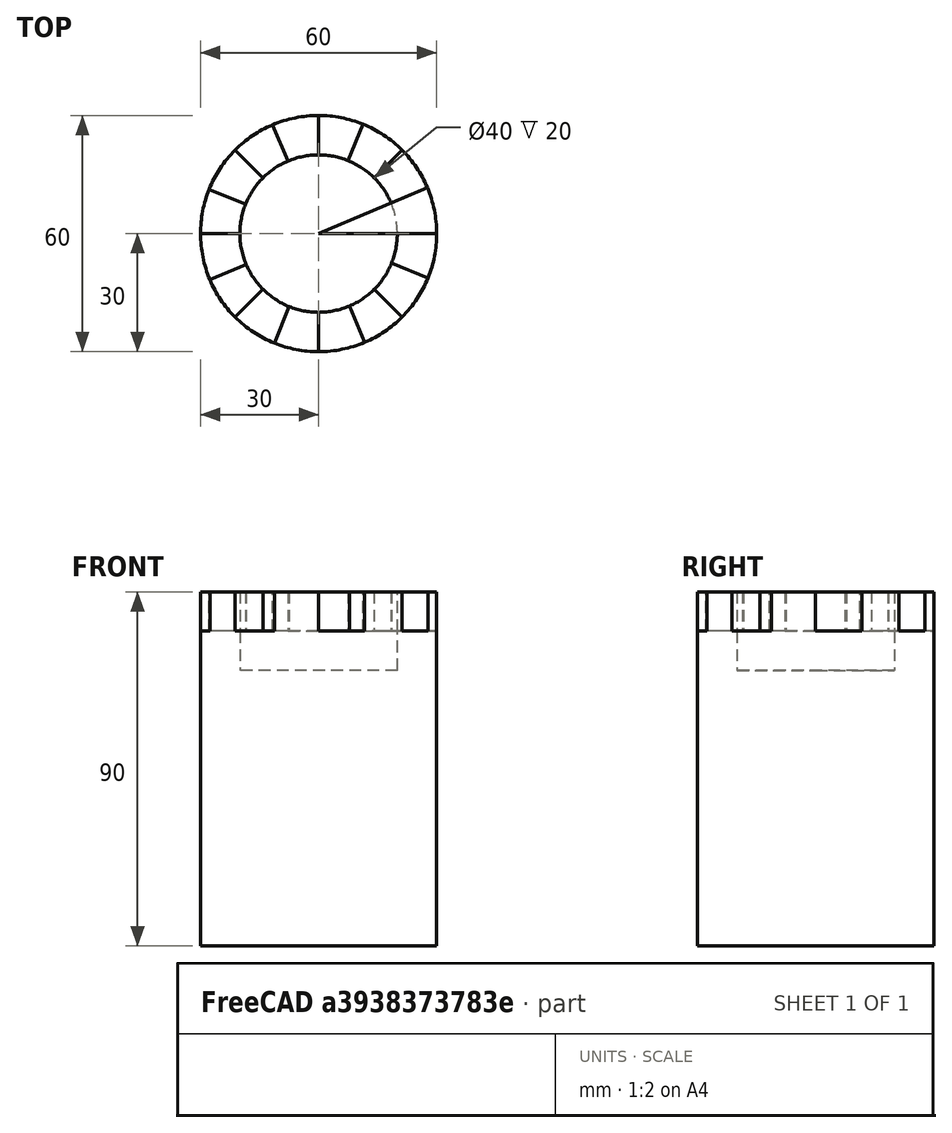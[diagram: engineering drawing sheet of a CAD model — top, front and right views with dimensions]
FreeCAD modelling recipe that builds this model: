
FCSTD DOCUMENT  (FreeCAD 0.21R33694 (Git))
Label: OJT1_T11R03_castell
License: All rights reserved
LicenseURL: http://en.wikipedia.org/wiki/All_rights_reserved
objects: Part::Cylinder×3, Part::Cut×2, Part::FeaturePython×1
note: 5 computed .brp shape members not serialized (recipe doc carries the construction recipe); baked Part::Feature solids carry a one-line shape summary decoded from their .brp

FEATURE [Part::Cylinder] Cylinder
  Angle = 360
  AttacherType = Attacher::AttachEngine3D
  FirstAngle = 0
  Height = 90
  Radius = 30
  SecondAngle = 0
FEATURE [Part::Cylinder] Cylinder001
  Angle = 23
  AttacherType = Attacher::AttachEngine3D
  FirstAngle = 0
  Height = 10
  Placement = pos=(0,0,80) rot=(0,0,1;0rad)
  Radius = 30
  SecondAngle = 0
FEATURE [Part::FeaturePython] Array  # Draft array (typed FeaturePython)
  AlwaysSyncPlacement = false
  Angle = 360
  ArrayType = 1
  Axis = (0,0,1)
  Base = -> Cylinder001
  Center = (0,0,0)
  Count = 8
  ExpandArray = false
  Fuse = false
  IntervalAxis = (0,0,0)
  IntervalX = (50,0,0)
  IntervalY = (0,50,0)
  IntervalZ = (0,0,50)
  NumberCircles = 3
  NumberPolar = 8
  NumberX = 2
  NumberY = 2
  NumberZ = 1
  PlacementList = 8 placements: [(0,0,80),(0,0,80),(0,0,80),(0,0,80),(0,0,80),(0,0,80),(0,0,80),(0,0,80)]
  RadialDistance = 50
  ScaleList = (8) [(1,1,1),(1,1,1),(1,1,1),(1,1,1),(1,1,1),(1,1,1),(1,1,1),(1,1,1)]
  Symmetry = 1
  TangentialDistance = 25
FEATURE [Part::Cut] Cut
  Base = -> Cylinder
  Refine = true
  Tool = -> Array
FEATURE [Part::Cylinder] Cylinder002
  Angle = 360
  AttacherType = Attacher::AttachEngine3D
  FirstAngle = 0
  Height = 20
  Placement = pos=(0,0,70) rot=(0,0,1;0rad)
  Radius = 20
  SecondAngle = 0
FEATURE [Part::Cut] Cut001
  Base = -> Cut
  Refine = true
  Tool = -> Cylinder002
